# Revit family: Haworth_BuzziPleat_Ripple_EU_PRELIMINARY
name_source: partatom
category: Furniture
revit_build: Autodesk Revit 2018 (Build: 20170223_1515(x64)
units: mm (PartAtom-declared; Revit-internal decimal feet)

## family parameters
Cut with Voids When Loaded = No
Host = Face
Room Calculation Point = No
Shared = No

## types (2) — shared parameters
Assembly Code = E2020200
Description = Haworth - BuzziPleat - Ripple
Manufacturer = Haworth
Max. Cable Length = 500 cm
Min. Cable Length = 25 cm
Model = Buzzi Pleat
Note = Verify Final Dim. w/ Haworth
Trim Finish = Haworth _ Paint _ Collection Black
URL = https://www.haworth.com
URL - Product = https://www.haworth.com
Warranty = https://www.haworth.com
zero-valued in all types: Default Elevation

## per-type parameters (varying)
| type | Actual Depth | Actual Height | Actual Width | Large | Medium |
| Large | 150 cm | 20 cm | 150 cm | Yes | No |
| Medium | 100 cm | 13 cm | 100 cm | No | Yes |

## geometry (parser evidence)
native form markers: Blend x4, Sweep x20
no freeform markers — native parametric forms only
